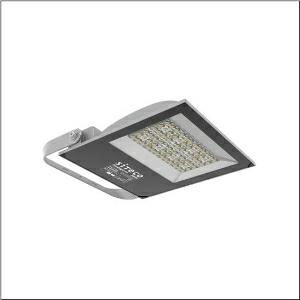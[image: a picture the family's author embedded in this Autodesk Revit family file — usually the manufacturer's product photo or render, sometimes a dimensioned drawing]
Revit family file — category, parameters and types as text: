
# Revit family: floodlight_fl_41_midi___pl32_5xa8581b2121_e0cb
name_source: partatom
category: Lighting Fixtures
units: mm (PartAtom-declared; Revit-internal decimal feet)

## family parameters
Cut with Voids When Loaded = No
Host = Face
Light Source = No
Part Type = Normal
Room Calculation Point = No
Round Connector Dimension = Use Diameter
Shared = No

## types (1)
- --- (1 x LED, 26000 lm, 200 W, 4000K)
    Apparent Load = 200 VA
    CIE Flux Codes = 38 75 98 100 100
    Color Rendering = 70
    Color Temperature = 4000K
    Default Elevation = 1800 mm
    Description = Floodlight FL 41 midi, floodlight, primary light control with lens, of PMMA, primary optical cover: protective disc, transparent, light distribution: PL32, light emission: direct distribution, installation type: surface-mounted, LED, High Power LED, rated luminous flux: 26.000lm, luminous efficacy: 130lm/W, light colour: 740, colour temperature: 4000K, control gear: ON/OFF Multilumen, with cable, 3x 1.5mm², mains connection: 220..240V, AC, 50/60Hz, connection cable pre-assembled, cable length: 2m, rated input power: 200W, luminaire housing, of diecast aluminium, powder-coated, metallic grey (RAL 9006), length: 375mm, width: 335mm, height: 65mm, protection rating (complete): IP65, insulation class (complete): insulation class I (protective earthing), certification: CE, ENEC, impact resistance: IK08, permissible operating ambient temperature: -40..+40°C, permissible storage temperature: -40..+60°C, packaging unit: 1 piece

Light Distribution: PL32
    Height = 66 mm
    Lamp = 1 x LED
    Lamp Light Flux = 26000 lm
    Lamp Power = 200 W
    Lamp count = 1
    Length = 323 mm
    Luminous efficacy = 130 lm/W
    Manufacturer = Siteco
    ModVariant = No
    Model = 5XA8581B2121
    Mounting Place = Ceiling
    Mounting Type = Surface mounted
    Number of Poles = 1
    OnlyDefault = Yes
    Power Factor = 1
    Product Name = Floodlight FL 41 midi | PL32
    Product group = floodlight | ceiling mounted
    ProductGroupID = 301
    Protection Class = Protection class I
    Protection Degree = IP 65
    RLX_Detail_Level = 1
    RLX_Emergency_Light_Flux = 0 lm
    RLX_Emergency_Type = 0
    RLX_Emergency_Type_DB = No
    RlxData = <blob elided: 27417 chars, md5=c524690b>
    Socket = socket
    Standby Power = 0 W
    System Light Flux = 26000 lm
    System Power = 200 W
    Type Comments = factory setting: luminous flux: 100 % | (OFF | OFF | OFF)
    Type Image = l_1248229.jpg
    URL = http://relux.com
    VarID = @adj_131656
    Voltage = 0 V
    Weight = 0.00 kg
    Width = 331 mm

## geometry (parser evidence)
native form markers: Blend x4, Sweep x9
no freeform markers — native parametric forms only
